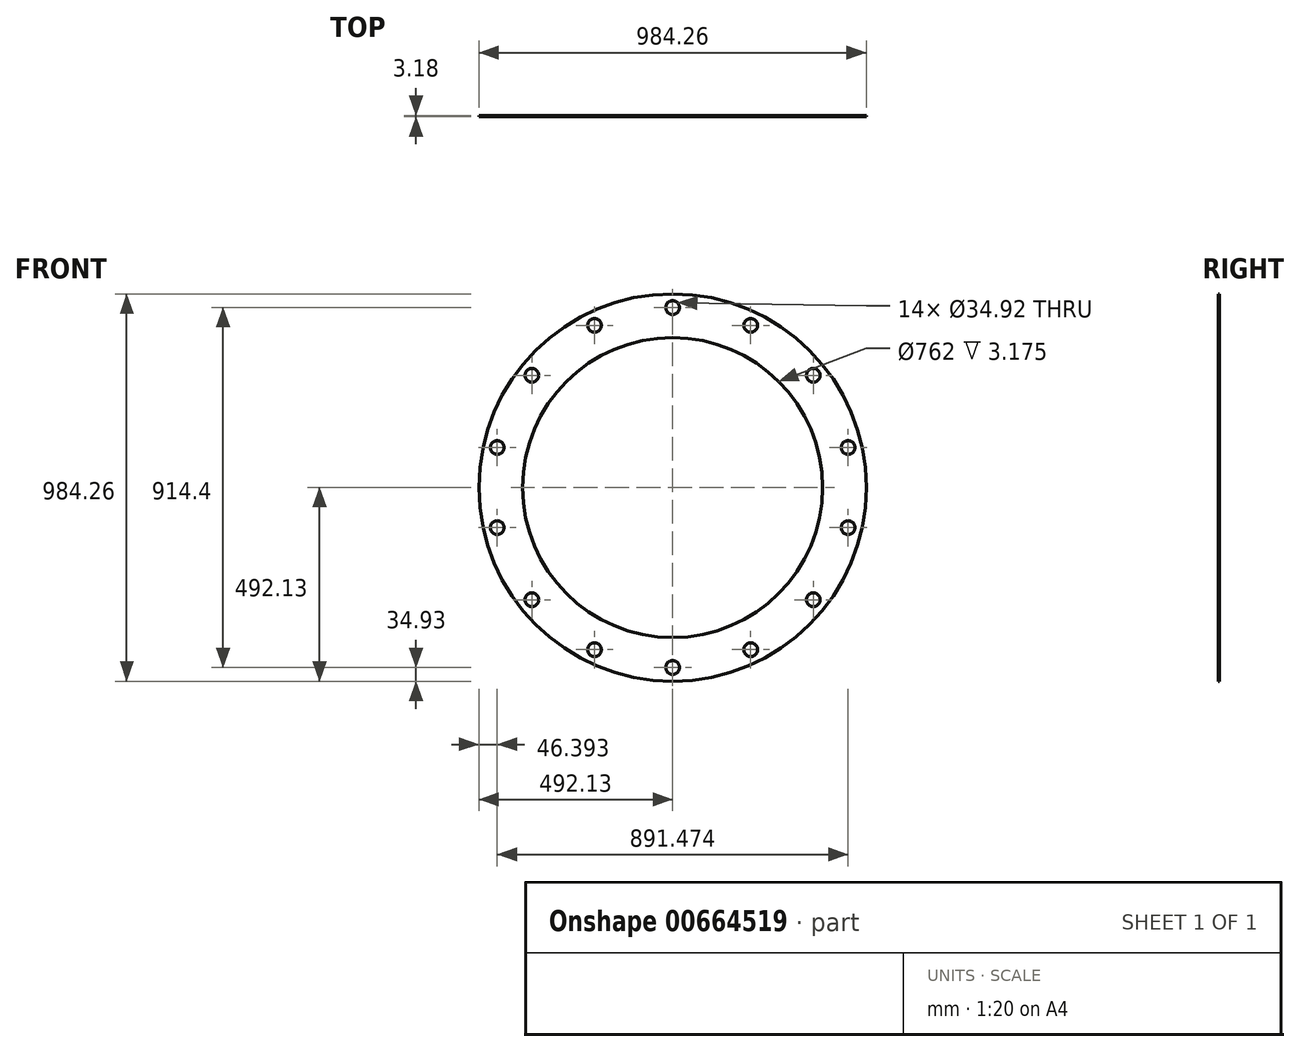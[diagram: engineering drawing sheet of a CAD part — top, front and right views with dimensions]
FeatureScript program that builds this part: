
annotation { "Feature Type Name" : "Feature", "Feature Type Description" : "" }
export const myFeature = defineFeature(function(context is Context, id is Id, definition is map)
    precondition{}
    {
        {
            var Q0;
            Q0=qCreatedBy(makeId("Front.planeOp"),FACE);
            var sketch = newSketch(context, id + "F0", { "sketchPlane" : qUnion([Q0])});
            skCircle(sketch, "E0", {"center": v(0, 0) * mm, "radius": 381 * mm});
            skCircle(sketch, "E1", {"center": v(0, 0) * mm, "radius": 492.13 * mm});
            skCircle(sketch, "E2", {"center": v(0, 0) * mm, "radius": 457.2 * mm, "construction": true});
            skCircle(sketch, "E3", {"center": v(0, 457.2) * mm, "radius": 17.46 * mm});
            skCircle(sketch, "E4.1.0", {"center": v(-198.37, 411.92) * mm, "radius": 17.46 * mm});
            skCircle(sketch, "E4.2.0", {"center": v(-357.45, 285.06) * mm, "radius": 17.46 * mm});
            skCircle(sketch, "E4.3.0", {"center": v(-445.74, 101.74) * mm, "radius": 17.46 * mm});
            skCircle(sketch, "E4.4.0", {"center": v(-445.74, -101.74) * mm, "radius": 17.46 * mm});
            skCircle(sketch, "E4.5.0", {"center": v(-357.45, -285.06) * mm, "radius": 17.46 * mm});
            skCircle(sketch, "E4.6.0", {"center": v(-198.37, -411.92) * mm, "radius": 17.46 * mm});
            skCircle(sketch, "E4.7.0", {"center": v(0, -457.2) * mm, "radius": 17.46 * mm});
            skCircle(sketch, "E4.8.0", {"center": v(198.37, -411.92) * mm, "radius": 17.46 * mm});
            skCircle(sketch, "E4.9.0", {"center": v(357.45, -285.06) * mm, "radius": 17.46 * mm});
            skCircle(sketch, "E4.10.0", {"center": v(445.74, -101.74) * mm, "radius": 17.46 * mm});
            skCircle(sketch, "E4.11.0", {"center": v(445.74, 101.74) * mm, "radius": 17.46 * mm});
            skCircle(sketch, "E4.12.0", {"center": v(357.45, 285.06) * mm, "radius": 17.46 * mm});
            skCircle(sketch, "E4.13.0", {"center": v(198.37, 411.92) * mm, "radius": 17.46 * mm});
            skSolve(sketch);
        }
        {
            var Q0;
            Q0=makeQuery(id+"F0.imprint","IMPRINT",FACE,{"disambiguationData":[TD([[makeQuery(id+"F0.imprint","IMPRINT",EDGE,{"derivedFrom":sQuery(id+"F0.wireOp",EDGE,"E0")}),-1.0]])]});
            extrude(context, id + "F1", {"entities" : qUnion([Q0]), "depth" : 3.17 * mm, "offsetDistance" : 25.4 * mm});
        }
    });
